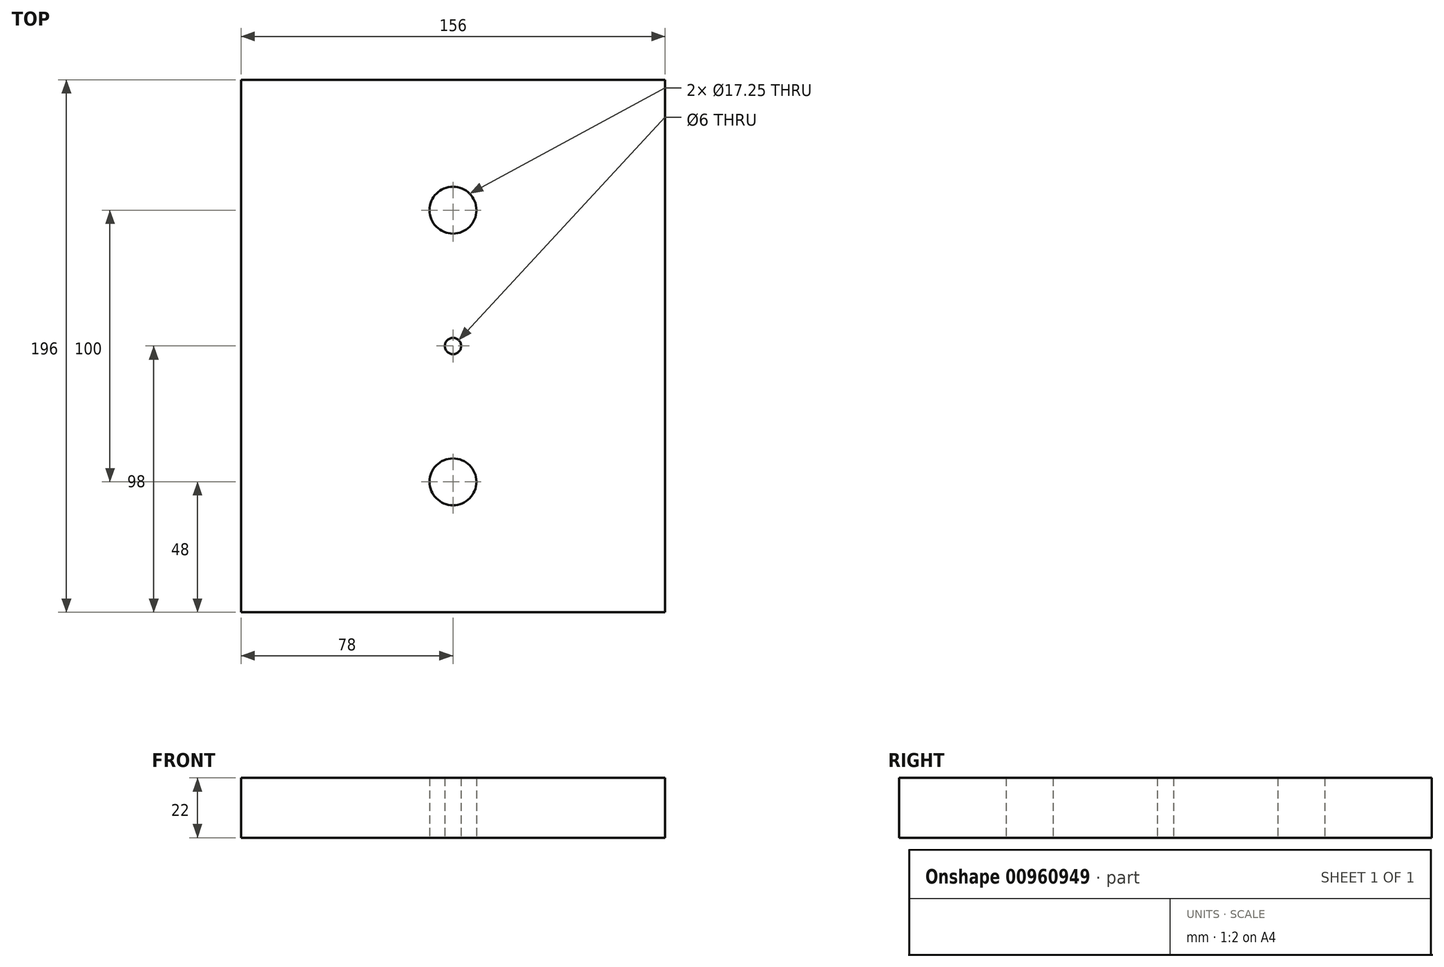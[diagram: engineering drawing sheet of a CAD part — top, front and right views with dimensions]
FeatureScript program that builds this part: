
annotation { "Feature Type Name" : "Feature", "Feature Type Description" : "" }
export const myFeature = defineFeature(function(context is Context, id is Id, definition is map)
    precondition{}
    {
        {
            var Q0;
            Q0=qCreatedBy(makeId("Top.planeOp"),FACE);
            var sketch = newSketch(context, id + "F0", { "sketchPlane" : qUnion([Q0])});
            skLineSegment(sketch, "E0.bottom", {"start": v(-78, 98) * mm, "end": v(78, 98) * mm});
            skLineSegment(sketch, "E0.top", {"start": v(-78, -98) * mm, "end": v(78, -98) * mm});
            skLineSegment(sketch, "E0.left", {"start": v(-78, 98) * mm, "end": v(-78, -98) * mm});
            skLineSegment(sketch, "E0.right", {"start": v(78, 98) * mm, "end": v(78, -98) * mm});
            skLineSegment(sketch, "E1", {"start": v(0, 98) * mm, "end": v(0, -98) * mm, "construction": true});
            skLineSegment(sketch, "E2", {"start": v(-78, 0) * mm, "end": v(78, 0) * mm, "construction": true});
            skCircle(sketch, "E3", {"center": v(0, 0) * mm, "radius": 3 * mm});
            skCircle(sketch, "E4", {"center": v(0, -50) * mm, "radius": 8.62 * mm});
            skCircle(sketch, "E5.MirrorC", {"center": v(0, 50) * mm, "radius": 8.62 * mm});
            skSolve(sketch);
        }
        {
            var Q0;
            Q0=makeQuery(id+"F0.imprint","IMPRINT",FACE,{"disambiguationData":[TD([[makeQuery(id+"F0.imprint","IMPRINT",EDGE,{"derivedFrom":sQuery(id+"F0.wireOp",EDGE,"E0.bottom")}),-1.0]])]});
            var Q1;
            Q1=sQuery(id+"F0.wireOp",EDGE,"E0.left");
            extrude(context, id + "F1", {"entities" : qUnion([Q0]), "surfaceEntities" : qUnion([Q1]), "depth" : 22 * mm, "offsetDistance" : 25 * mm});
        }
    });
